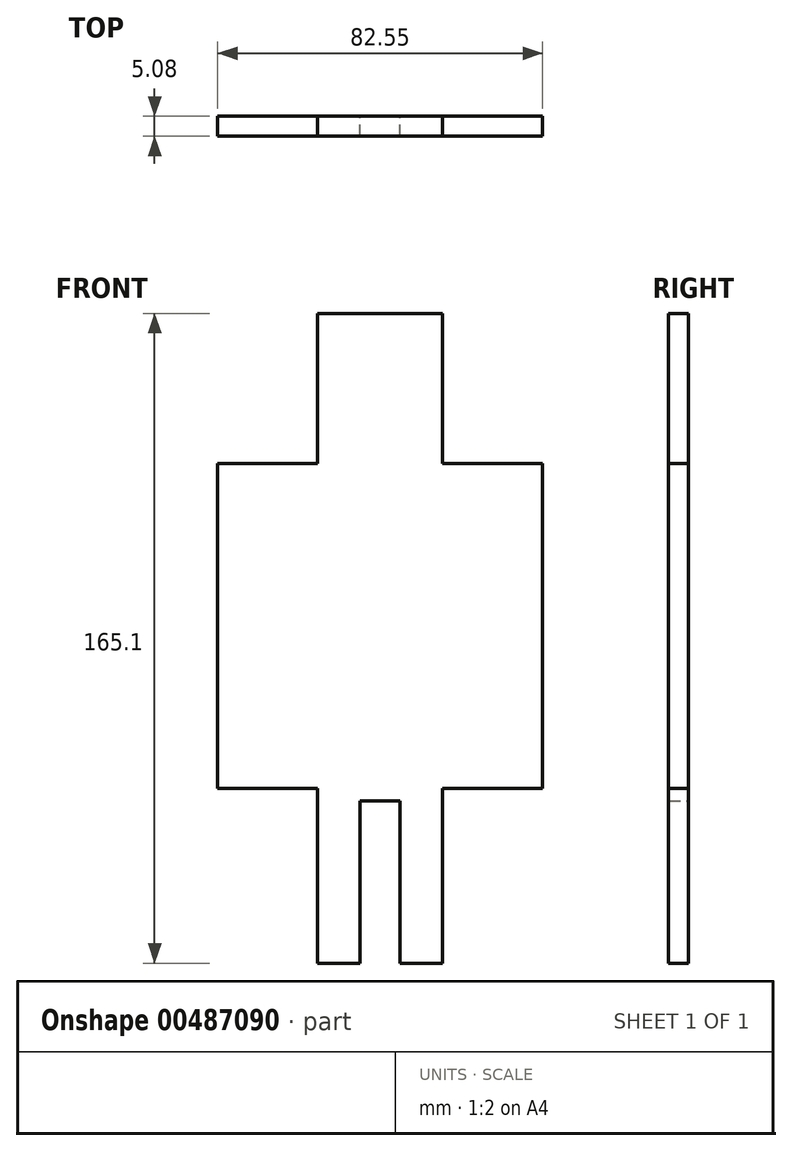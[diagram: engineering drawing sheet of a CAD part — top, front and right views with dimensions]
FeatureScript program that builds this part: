
annotation { "Feature Type Name" : "Feature", "Feature Type Description" : "" }
export const myFeature = defineFeature(function(context is Context, id is Id, definition is map)
    precondition{}
    {
        {
            var Q0;
            Q0=qCreatedBy(makeId("Front.planeOp"),FACE);
            var sketch = newSketch(context, id + "F0", { "sketchPlane" : qUnion([Q0])});
            skLineSegment(sketch, "E0", {"start": v(5.1, 56.03) * mm, "end": v(36.86, 56.03) * mm});
            skLineSegment(sketch, "E1", {"start": v(36.86, 56.03) * mm, "end": v(36.86, 17.93) * mm});
            skLineSegment(sketch, "E2", {"start": v(36.86, 17.93) * mm, "end": v(62.26, 17.93) * mm});
            skLineSegment(sketch, "E3", {"start": v(62.26, 17.93) * mm, "end": v(62.26, -64.62) * mm});
            skLineSegment(sketch, "E4", {"start": v(62.26, -64.62) * mm, "end": v(36.86, -64.62) * mm});
            skLineSegment(sketch, "E5", {"start": v(36.86, -64.62) * mm, "end": v(36.86, -109.07) * mm});
            skLineSegment(sketch, "E6", {"start": v(36.86, -109.07) * mm, "end": v(26.06, -109.07) * mm});
            skLineSegment(sketch, "E7", {"start": v(5.1, -109.07) * mm, "end": v(5.1, -64.62) * mm});
            skLineSegment(sketch, "E8", {"start": v(5.1, -64.62) * mm, "end": v(-20.3, -64.62) * mm});
            skLineSegment(sketch, "E9", {"start": v(-20.3, -64.62) * mm, "end": v(-20.3, 17.93) * mm});
            skLineSegment(sketch, "E10", {"start": v(-20.3, 17.93) * mm, "end": v(5.1, 17.93) * mm});
            skLineSegment(sketch, "E11", {"start": v(5.1, 17.93) * mm, "end": v(5.1, 56.03) * mm});
            skPoint(sketch, "E12.orphan", {"position": v(-26.64, 56.03) * mm});
            skLineSegment(sketch, "E13", {"start": v(5.1, -109.07) * mm, "end": v(15.9, -109.07) * mm});
            skLineSegment(sketch, "E14", {"start": v(15.9, -109.07) * mm, "end": v(15.9, -67.8) * mm});
            skLineSegment(sketch, "E15", {"start": v(15.9, -67.8) * mm, "end": v(26.06, -67.8) * mm});
            skLineSegment(sketch, "E16", {"start": v(26.06, -67.8) * mm, "end": v(26.06, -109.07) * mm});
            skLineSegment(sketch, "E17.trimOffspring", {"start": v(15.9, -109.07) * mm, "end": v(5.1, -109.07) * mm});
            skSolve(sketch);
        }
        {
            var Q0;
            Q0 = qSketchRegion(id + "F0", true);
            extrude(context, id + "F1", {"entities" : qUnion([Q0]), "depth" : 5.08 * mm});
        }
    });
